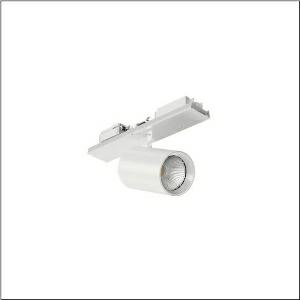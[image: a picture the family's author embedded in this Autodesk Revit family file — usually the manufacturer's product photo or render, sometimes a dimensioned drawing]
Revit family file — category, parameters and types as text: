
# Revit family: licross_r__spot_31_51sl137a45b_29a8
name_source: partatom
category: Lighting Fixtures
units: mm (PartAtom-declared; Revit-internal decimal feet)

## family parameters
Cut with Voids When Loaded = No
Host = Face
Light Source = No
Part Type = Normal
Room Calculation Point = No
Round Connector Dimension = Use Diameter
Shared = No

## types (1)
- --- (1 x LED, 5190 lm, 42.6 W, 4000K)
    Apparent Load = 43 VA
    CIE Flux Codes = 92 97 99 100 100
    Color Rendering = 90
    Color Temperature = 4000K
    Default Elevation = 1800 mm
    Description = Licross® Spot 31, directional spotlight, light control with lens, of plastic, LED rated luminous flux: 5.190lm, light colour: 940, with plug, 3-pole, with phase selection, mains connection: 220..240V, AC, 50/60Hz, of aluminium, traffic white (RAL 9016), length: 300mm, diameter: 90mm, protection rating (complete): IP20, insulation class (complete): insulation class I (protective earthing), certification: CE, packaging unit: 1 piece
    Height = 175 mm
    Lamp = 1 x LED
    Lamp Light Flux = 5190 lm
    Lamp Power = 42.6 W
    Lamp count = 1
    Length = 90 mm
    Luminous efficacy = 122 lm/W
    Manufacturer = Siteco
    ModVariant = No
    Model = 51SL137A45B
    Mounting Place = Ceiling
    Mounting Type = Pendant
    Number of Poles = 1
    OnlyDefault = Yes
    Power Factor = 1
    Product Name = Licross® Spot 31
    Product group = directional spotlight
    ProductGroupID = 906
    Protection Class = Protection class I
    Protection Degree = IP 20
    RLX_Detail_Level = 1
    RLX_Emergency_Light_Flux = 0 lm
    RLX_Emergency_Type = 0
    RLX_Emergency_Type_DB = No
    RlxData = <blob elided: 14801 chars, md5=0143a798>
    Socket = socket
    Standby Power = 0 W
    System Light Flux = 5190 lm
    System Power = 43 W
    Type Comments = factory setting: luminous flux: 100 % | (ON | ON | ON) | 1050 mA
    Type Image = l_1245720.jpg
    URL = http://relux.com
    VarID = @adj_132328
    Voltage = 0 V
    Weight = 0.00 kg
    Width = 0 mm  [stored 0 ft]

note: [stored X ft] marks values corroborated as IEEE doubles in the binary element streams (Revit-internal decimal feet)

## geometry (parser evidence)
native form markers: Sweep x12
no freeform markers — native parametric forms only
